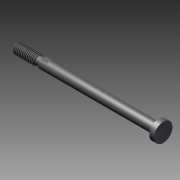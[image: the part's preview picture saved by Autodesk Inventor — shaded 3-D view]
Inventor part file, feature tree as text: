
AUTODESK INVENTOR PART (.ipt)
format: ipt  version: 2011 SP1 (Build 150282100, 282)  size: 106,496 bytes
history: native  units: mm
features: other x21, sketch x2, revolve x1, thread x1, extrude x1
ambient origin geometry x8: Origin, YZ Plane, XZ Plane, XY Plane, X Axis, Y Axis, Z Axis, Center Point
bodies: Solid1 (feature_tree)
feature tree (26):
  revolve  "Revolution1"  [1 undecoded]
  thread  "Thread1"  [1 undecoded]
  extrude  "Extrusion1"  [1 undecoded]
  other  "P1_XY"
  other  "P1_YZ"
  other  "P1_ZX"
  other  "P1_X"
  other  "P1_Y"
  other  "P1_Z"
  other  "P1_Center"
  other  "PD1_XY"
  other  "PD1_YZ"
  other  "PD1_ZX"
  other  "PD1_X"
  other  "PD1_Y"
  other  "PD1_Z"
  other  "PD1_Center"
  other  "PD2_XY"
  other  "PD2_YZ"
  other  "PD2_ZX"
  other  "PD2_X"
  other  "PD2_Y"
  other  "PD2_Z"
  other  "PD2_Center"
  sketch  "Skizze_1"  dims[d0=360.0deg d1=12.373mm d2=0.0mm d3=4.0mm d4=0.0mm]
  sketch  "Skizze_4"
note: 3 required parameter values undecoded (feature->parameter linkage not recoverable at this tier; creation-order binding heuristic only, values carry confidence <= 0.55)